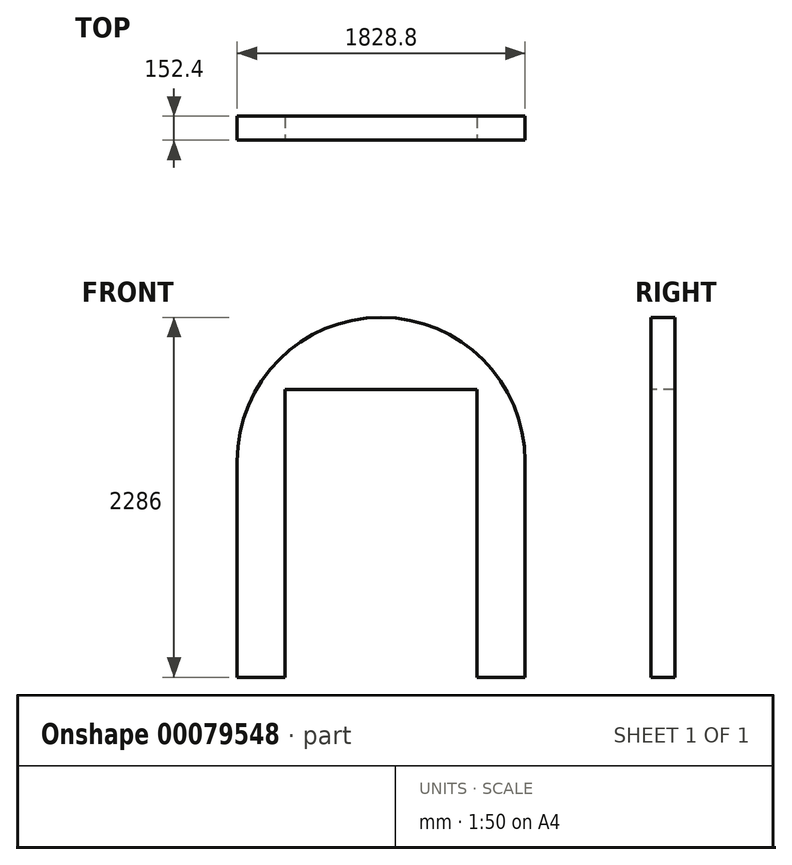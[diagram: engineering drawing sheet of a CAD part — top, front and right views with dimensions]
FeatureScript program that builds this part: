
annotation { "Feature Type Name" : "Feature", "Feature Type Description" : "" }
export const myFeature = defineFeature(function(context is Context, id is Id, definition is map)
    precondition{}
    {
        {
            var Q0;
            Q0=qCreatedBy(makeId("Front.planeOp"),FACE);
            var sketch = newSketch(context, id + "F0", { "sketchPlane" : qUnion([Q0])});
            skLineSegment(sketch, "E0", {"start": v(-962.47, -1309.37) * mm, "end": v(-962.47, 62.23) * mm});
            skLineSegment(sketch, "E1", {"start": v(-962.47, -1309.37) * mm, "end": v(866.33, -1309.37) * mm});
            skLineSegment(sketch, "E2", {"start": v(866.33, -1309.37) * mm, "end": v(866.33, 62.23) * mm});
            skArc(sketch, "E3", {"start": v(-962.47, 62.23) * mm, "mid": v(-48.07, 976.63) * mm, "end": v(866.33, 62.23) * mm});
            skPoint(sketch, "E3.centerSnap0", {"position": v(-48.07, -1309.37) * mm});
            skSolve(sketch);
        }
        {
            var Q0;
            Q0=makeQuery(id+"F0.imprint","IMPRINT",FACE,{"disambiguationData":[TD([[makeQuery(id+"F0.imprint","IMPRINT",EDGE,{"derivedFrom":sQuery(id+"F0.wireOp",EDGE,"E0")}),-1.0]])]});
            extrude(context, id + "F1", {"entities" : qUnion([Q0]), "depth" : 152.4 * mm});
        }
        {
            var Q0;
            Q0=makeQuery(id+"F1.opExtrude","CAP_FACE",FACE,{"disambiguationData":[OSD([sQuery(id+"F0.wireOp",EDGE,"E0"),sQuery(id+"F0.wireOp",EDGE,"E1"),sQuery(id+"F0.wireOp",EDGE,"E2"),sQuery(id+"F0.wireOp",EDGE,"E3")])],"isStart":false});
            var sketch = newSketch(context, id + "F2", { "sketchPlane" : qUnion([Q0])});
            skLineSegment(sketch, "E4", {"start": v(-657.67, -1309.37) * mm, "end": v(-657.67, 519.43) * mm});
            skLineSegment(sketch, "E5", {"start": v(561.53, -1309.37) * mm, "end": v(561.53, 519.43) * mm});
            skLineSegment(sketch, "E6", {"start": v(-657.67, 519.43) * mm, "end": v(561.53, 519.43) * mm});
            skSolve(sketch);
        }
        {
            var Q0;
            {var subQ0=sQuery(id+"F2.wireOp",EDGE,"E4");Q0=makeQuery(id+"F2.imprint","IMPRINT",FACE,{"disambiguationData":[TD([[makeQuery(id+"F2.imprint","IMPRINT",EDGE,{"derivedFrom":subQ0}),-1.0]])]});}
            extrude(context, id + "F3", {"entities" : qUnion([Q0]), "operationType" : NewBodyOperationType.REMOVE, "oppositeDirection" : true, "depth" : 25.4 * mm});
        }
        {
            var Q0;
            {var subQ0=sQuery(id+"F2.wireOp",EDGE,"E4");Q0=makeQuery(id+"F2.imprint","IMPRINT",FACE,{"disambiguationData":[TD([[makeQuery(id+"F2.imprint","IMPRINT",EDGE,{"derivedFrom":subQ0}),-1.0]])]});}
            extrude(context, id + "F4", {"entities" : qUnion([Q0]), "operationType" : NewBodyOperationType.REMOVE, "endBound" : BoundingType.THROUGH_ALL, "oppositeDirection" : true, "depth" : 12700 * mm});
        }
    });
